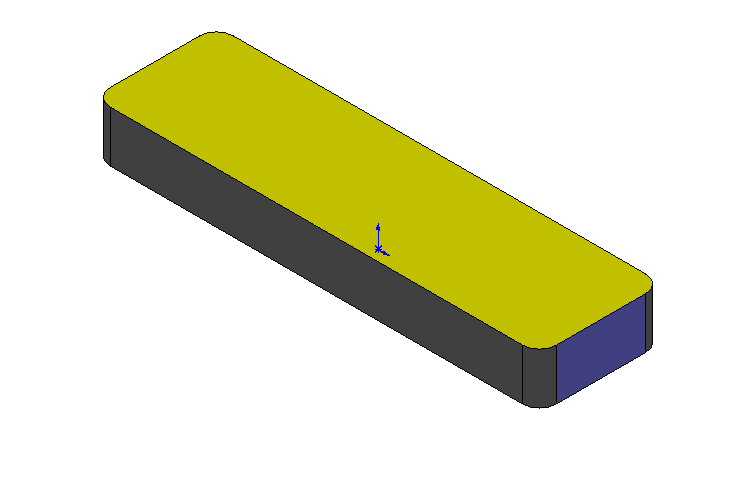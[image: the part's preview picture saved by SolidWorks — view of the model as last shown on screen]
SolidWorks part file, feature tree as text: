
SOLIDWORKS PART (.sldprt)
format: sldprt  version: not decoded by parser v0  size: 210,432 bytes
history: native  units: mm
features: plane x3, sketch x3, material x1, extrude x1, revolve x1, mirror x1, cut_extrude x1 (+10 scaffold rows collapsed)
feature tree (21):
  scaffold x10  (default folders/planes/origin — collapsed)
  material  "Matériau <non spécifié>"
  plane  "Plan de face"
  plane  "Plan de dessus"
  plane  "Plan de droite"
  sketch  "Esquisse1"  dims[D3=2.0mm D1=52.5mm D2=14.5mm]
  extrude  "Extrusion1"  Depth=6mm
  sketch  "Esquisse6"  dims[D1=24.0mm D2=5.0mm D3=5.0mm D4=6.0mm D5=3.5mm D6=3.5mm D7=~25.042088mm]
  revolve  "Révolution1"  Angle=360deg
  mirror  "Symétrie1"
  sketch  "Esquisse7"  dims[D1=1.0mm]
  cut_extrude  "Enlèv. mat.-Extru.1"  [1 undecoded]
decode coverage: 5 of 7 modeling features carry decoded parameters
note: ~ marks probable driven/reference dimensions
note: 1 parameter value undecoded
note: suppression state not decoded; provenance and decode notes live in map.json
